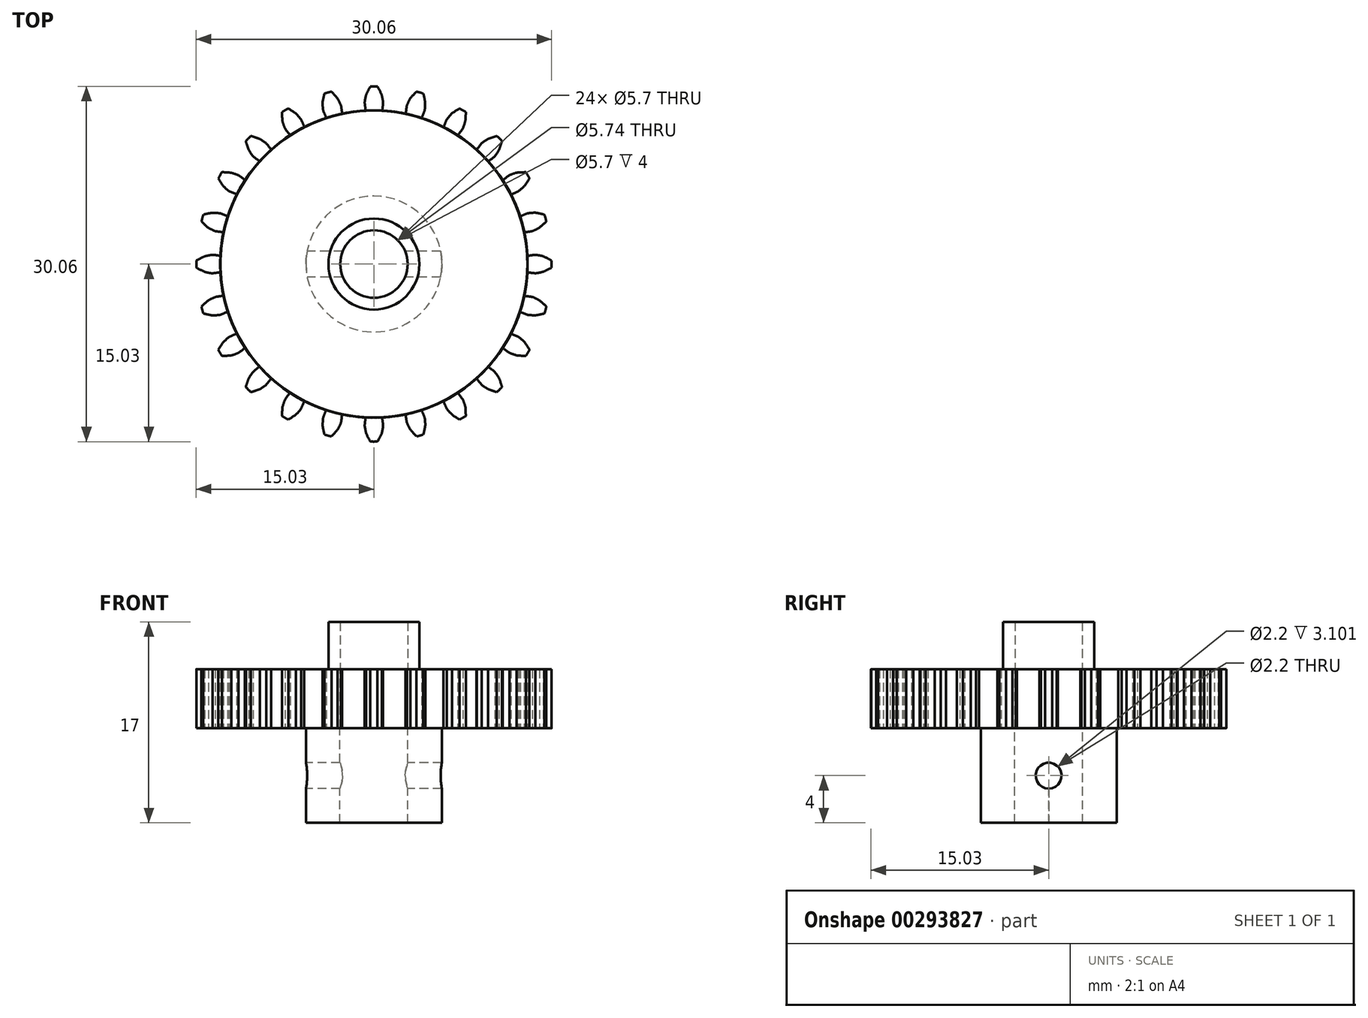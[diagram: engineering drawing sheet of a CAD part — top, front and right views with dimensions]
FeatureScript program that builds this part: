
annotation { "Feature Type Name" : "Feature", "Feature Type Description" : "" }
export const myFeature = defineFeature(function(context is Context, id is Id, definition is map)
    precondition{}
    {
        {
            var Q0;
            Q0=qCreatedBy(makeId("Top.planeOp"),FACE);
            var sketch = newSketch(context, id + "F0", { "sketchPlane" : qUnion([Q0])});
            skCircle(sketch, "E0", {"center": v(0, 0) * mm, "radius": 16 * mm, "construction": true});
            skCircle(sketch, "E1", {"center": v(0, 0) * mm, "radius": 15 * mm, "construction": true});
            skCircle(sketch, "E2", {"center": v(0, 0) * mm, "radius": 13 * mm});
            skLineSegment(sketch, "E3", {"start": v(0, 0) * mm, "end": v(0, 15.03) * mm, "construction": true});
            skLineSegment(sketch, "E4", {"start": v(0, 16) * mm, "end": v(0, 16) * mm});
            skPoint(sketch, "E5.start.orphan", {"position": v(2.17, 12.82) * mm});
            skLineSegment(sketch, "E6", {"start": v(2.83, 2.38) * mm, "end": v(2.83, 2.38) * mm});
            skPoint(sketch, "E7.orphan", {"position": v(2.17, 12.9) * mm});
            skArc(sketch, "E8", {"start": v(0.3, 7.97) * mm, "mid": v(0, 7.98) * mm, "end": v(-0.3, 7.97) * mm});
            skArc(sketch, "E9", {"start": v(-0.3, 7.97) * mm, "mid": v(-0.5, 7.63) * mm, "end": v(-0.67, 7.27) * mm});
            skArc(sketch, "E10", {"start": v(0.65, 7.27) * mm, "mid": v(0.49, 7.63) * mm, "end": v(0.3, 7.97) * mm});
            skArc(sketch, "E11", {"start": v(-0.78, 6.64) * mm, "mid": v(-0.74, 6.3) * mm, "end": v(-0.7, 5.95) * mm});
            skArc(sketch, "E12", {"start": v(0.7, 5.95) * mm, "mid": v(0.75, 6.3) * mm, "end": v(0.78, 6.64) * mm});
            skArc(sketch, "E13", {"start": v(-0.67, 7.27) * mm, "mid": v(-0.73, 6.96) * mm, "end": v(-0.78, 6.64) * mm});
            skArc(sketch, "E14", {"start": v(0.78, 6.64) * mm, "mid": v(0.72, 6.96) * mm, "end": v(0.65, 7.28) * mm});
            skArc(sketch, "E15", {"start": v(0.3, 15.02) * mm, "mid": v(0, 15.03) * mm, "end": v(-0.3, 15.02) * mm});
            skArc(sketch, "E16", {"start": v(-0.3, 15.02) * mm, "mid": v(-0.5, 14.67) * mm, "end": v(-0.66, 14.32) * mm});
            skArc(sketch, "E17", {"start": v(0.66, 14.32) * mm, "mid": v(0.49, 14.67) * mm, "end": v(0.3, 15.02) * mm});
            skArc(sketch, "E18", {"start": v(-0.78, 13.68) * mm, "mid": v(-0.74, 13.34) * mm, "end": v(-0.69, 13) * mm});
            skArc(sketch, "E19", {"start": v(0.7, 13) * mm, "mid": v(0.75, 13.34) * mm, "end": v(0.78, 13.68) * mm});
            skArc(sketch, "E20", {"start": v(-0.66, 14.32) * mm, "mid": v(-0.73, 14) * mm, "end": v(-0.78, 13.68) * mm});
            skArc(sketch, "E21", {"start": v(0.78, 13.68) * mm, "mid": v(0.72, 14) * mm, "end": v(0.66, 14.32) * mm});
            skLineSegment(sketch, "E22", {"start": v(-0.69, 13) * mm, "end": v(-0.69, 12.82) * mm});
            skLineSegment(sketch, "E23", {"start": v(-0.69, 12.82) * mm, "end": v(0.66, 12.82) * mm});
            skLineSegment(sketch, "E24", {"start": v(0.66, 12.82) * mm, "end": v(0.7, 13) * mm});
            skSolve(sketch);
        }
        {
            var Q0;
            Q0=qSketchRegion(id+"F0",true);
            extrude(context, id + "F1", {"entities" : qUnion([Q0]), "depth" : 5 * mm});
        }
        {
            var Q0;
            Q0=makeQuery(id+"F1.opExtrude","SWEPT_BODY",BODY,{"disambiguationData":[OSD([sQuery(id+"F0.wireOp",EDGE,"E2"),sQuery(id+"F0.wireOp",EDGE,"R10gV2s1-wa6S-ReX8-q8LX-GHZ9r4Q0mHum"),sQuery(id+"F0.wireOp",EDGE,"E5"),sQuery(id+"F0.wireOp",EDGE,"z46FLetc-xW6y-L8c0-6a1y-uqtfdu8xZMIJ"),sQuery(id+"F0.wireOp",EDGE,"9gFtCGWU-ELNh-Ofm0-j5xf-O9UD2OH31ImL"),sQuery(id+"F0.wireOp",EDGE,"cFb6o6lt-MkCW-7zTh-S24X-YUxYQt905Opy")])]});
            var Q1;
            Q1=makeQuery(id+"F1.opExtrude","SWEPT_FACE",FACE,{"disambiguationData":[OSD([sQuery(id+"F0.wireOp",EDGE,"E2")])]});
            circularPattern(context, id + "F2", {"entities" : qUnion([Q0]), "axis" : qUnion([Q1]), "angle" : 360 * degree, "instanceCount" : 24, "equalSpace" : true});
        }
        {
            var Q0;
            Q0=makeQuery(id+"F1.opExtrude","CAP_FACE",FACE,{"disambiguationData":[OSD([sQuery(id+"F0.wireOp",EDGE,"E2"),sQuery(id+"F0.wireOp",EDGE,"R10gV2s1-wa6S-ReX8-q8LX-GHZ9r4Q0mHum"),sQuery(id+"F0.wireOp",EDGE,"E5"),sQuery(id+"F0.wireOp",EDGE,"z46FLetc-xW6y-L8c0-6a1y-uqtfdu8xZMIJ"),sQuery(id+"F0.wireOp",EDGE,"9gFtCGWU-ELNh-Ofm0-j5xf-O9UD2OH31ImL"),sQuery(id+"F0.wireOp",EDGE,"cFb6o6lt-MkCW-7zTh-S24X-YUxYQt905Opy")])],"isStart":false});
            var sketch = newSketch(context, id + "F3", { "sketchPlane" : qUnion([Q0])});
            skCircle(sketch, "E25", {"center": v(0, 0) * mm, "radius": 2.85 * mm});
            skSolve(sketch);
        }
        {
            var Q0;
            Q0=qSketchRegion(id+"F3",true);
            extrude(context, id + "F4", {"entities" : qUnion([Q0]), "operationType" : NewBodyOperationType.REMOVE, "oppositeDirection" : true, "depth" : 25 * mm});
        }
        {
            var Q0;
            Q0=makeQuery(id+"F2.opPattern","COPY",FACE,{"derivedFrom":makeQuery(id+"F1.opExtrude","CAP_FACE",FACE,{"disambiguationData":[OSD([sQuery(id+"F0.wireOp",EDGE,"E2"),sQuery(id+"F0.wireOp",EDGE,"R10gV2s1-wa6S-ReX8-q8LX-GHZ9r4Q0mHum"),sQuery(id+"F0.wireOp",EDGE,"E5"),sQuery(id+"F0.wireOp",EDGE,"z46FLetc-xW6y-L8c0-6a1y-uqtfdu8xZMIJ"),sQuery(id+"F0.wireOp",EDGE,"9gFtCGWU-ELNh-Ofm0-j5xf-O9UD2OH31ImL"),sQuery(id+"F0.wireOp",EDGE,"cFb6o6lt-MkCW-7zTh-S24X-YUxYQt905Opy")])],"isStart":false}),"instanceName":"7"});
            var sketch = newSketch(context, id + "F5", { "sketchPlane" : qUnion([Q0])});
            skCircle(sketch, "E26", {"center": v(0, 0) * mm, "radius": 2.85 * mm});
            skCircle(sketch, "E27", {"center": v(0, 0) * mm, "radius": 3.85 * mm});
            skSolve(sketch);
        }
        {
            var Q0;
            Q0=qSketchRegion(id+"F5",true);
            extrude(context, id + "F6", {"entities" : qUnion([Q0]), "depth" : 4 * mm});
        }
        {
            var Q0;
            Q0=makeQuery(id+"F2.opPattern","COPY",FACE,{"derivedFrom":makeQuery(id+"F1.opExtrude","CAP_FACE",FACE,{"disambiguationData":[OSD([sQuery(id+"F0.wireOp",EDGE,"E2"),sQuery(id+"F0.wireOp",EDGE,"E15"),sQuery(id+"F0.wireOp",EDGE,"E16"),sQuery(id+"F0.wireOp",EDGE,"E17"),sQuery(id+"F0.wireOp",EDGE,"E18"),sQuery(id+"F0.wireOp",EDGE,"E19"),sQuery(id+"F0.wireOp",EDGE,"E20"),sQuery(id+"F0.wireOp",EDGE,"E21"),sQuery(id+"F0.wireOp",EDGE,"E22"),sQuery(id+"F0.wireOp",EDGE,"E24")])],"isStart":true}),"instanceName":"3"});
            var sketch = newSketch(context, id + "F7", { "sketchPlane" : qUnion([Q0])});
            skCircle(sketch, "E28", {"center": v(0, 0) * mm, "radius": 2.87 * mm});
            skCircle(sketch, "E29", {"center": v(0, 0) * mm, "radius": 5.75 * mm});
            skSolve(sketch);
        }
        {
            var Q0;
            Q0 = qSketchRegion(id + "F7", true);
            extrude(context, id + "F8", {"entities" : qUnion([Q0]), "depth" : 8 * mm});
        }
        {
            var Q0;
            Q0=makeQuery(id+"F8.opExtrude","CAP_FACE",FACE,{"disambiguationData":[OSD([sQuery(id+"F7.wireOp",EDGE,"E28"),sQuery(id+"F7.wireOp",EDGE,"E29")])],"isStart":false});
            var sketch = newSketch(context, id + "F9", { "sketchPlane" : qUnion([Q0])});
            skLineSegment(sketch, "E30", {"start": v(-5.75, 0) * mm, "end": v(-5.75, 0) * mm});
            skLineSegment(sketch, "E31", {"start": v(-5.75, 0) * mm, "end": v(-5.75, 0) * mm});
            skLineSegment(sketch, "E32", {"start": v(-5.75, 0) * mm, "end": v(-5.75, 0) * mm});
            skLineSegment(sketch, "E33", {"start": v(-5.75, 0) * mm, "end": v(-5.75, 0) * mm});
            skSolve(sketch);
        }
        {
            var Q0;
            Q0 = qSketchRegion(id + "F9", true);
            extrude(context, id + "F10", {"entities" : qUnion([Q0]), "operationType" : NewBodyOperationType.ADD, "oppositeDirection" : true, "depth" : 4 * mm});
        }
        {
            var Q0;
            Q0 = qSketchRegion(id + "F9", true);
            var Q1;
            Q1=makeQuery(id+"F10.boolean.opBoolean","MERGE",FACE,{"derivedFrom":[makeQuery(id+"F8.opExtrude","CAP_FACE",FACE,{"disambiguationData":[OSD([sQuery(id+"F7.wireOp",EDGE,"E28"),sQuery(id+"F7.wireOp",EDGE,"E29")])],"isStart":false}),makeQuery(id+"F10.opExtrude","CAP_FACE",FACE,{"disambiguationData":[OSD([sQuery(id+"F9.wireOp",EDGE,"E30"),sQuery(id+"F9.wireOp",EDGE,"E30"),sQuery(id+"F9.wireOp",EDGE,"E31"),sQuery(id+"F9.wireOp",EDGE,"E32"),sQuery(id+"F9.wireOp",EDGE,"E33")])],"isStart":true})]});
            extrude(context, id + "F11", {"entities" : qUnion([Q0, Q1]), "operationType" : NewBodyOperationType.ADD, "oppositeDirection" : true, "depth" : 4 * mm});
        }
        {
            var Q0;
            Q0=makeQuery(id+"F10.opExtrude","SWEPT_FACE",FACE,{"disambiguationData":[OSD([sQuery(id+"F9.wireOp",EDGE,"E32")])]});
            var sketch = newSketch(context, id + "F12", { "sketchPlane" : qUnion([Q0])});
            skCircle(sketch, "E34", {"center": v(0, -4) * mm, "radius": 1.1 * mm});
            skSolve(sketch);
        }
        {
            var Q0;
            Q0 = qSketchRegion(id + "F12", true);
            extrude(context, id + "F13", {"entities" : qUnion([Q0]), "operationType" : NewBodyOperationType.REMOVE, "oppositeDirection" : true, "depth" : 25 * mm});
        }
    });
